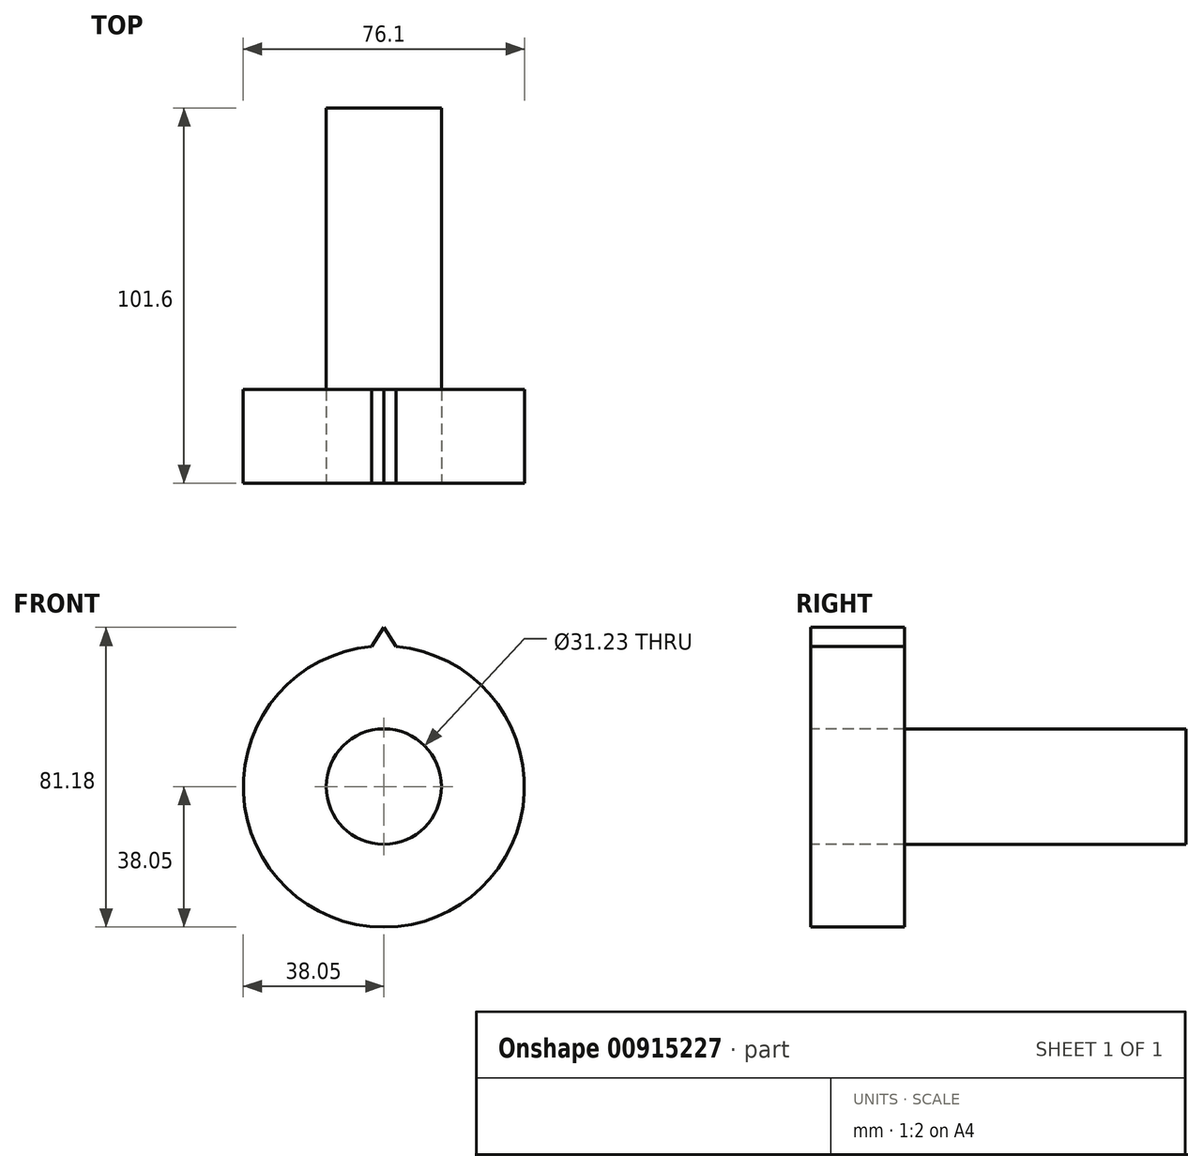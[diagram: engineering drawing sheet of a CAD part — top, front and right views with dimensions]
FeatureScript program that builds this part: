
annotation { "Feature Type Name" : "Feature", "Feature Type Description" : "" }
export const myFeature = defineFeature(function(context is Context, id is Id, definition is map)
    precondition{}
    {
        {
            var Q0;
            Q0=qCreatedBy(makeId("Front.planeOp"),FACE);
            var sketch = newSketch(context, id + "F0", { "sketchPlane" : qUnion([Q0])});
            skCircle(sketch, "E0", {"center": v(0, 0) * mm, "radius": 15.61 * mm});
            skSolve(sketch);
        }
        {
            var Q0;
            Q0 = qSketchRegion(id + "F0", true);
            extrude(context, id + "F1", {"entities" : qUnion([Q0]), "depth" : 101.6 * mm, "offsetDistance" : 25.4 * mm});
        }
        {
            var Q0;
            Q0=makeQuery(id+"F1.opExtrude","CAP_FACE",FACE,{"disambiguationData":[OSD([sQuery(id+"F0.wireOp",EDGE,"E0")])],"isStart":false});
            var sketch = newSketch(context, id + "F2", { "sketchPlane" : qUnion([Q0])});
            skCircle(sketch, "E1", {"center": v(0, 0) * mm, "radius": 15.61 * mm});
            skCircle(sketch, "E2", {"center": v(0, 0) * mm, "radius": 38.05 * mm});
            skSolve(sketch);
        }
        {
            var Q0;
            Q0=makeQuery(id+"F2.imprint","IMPRINT",FACE,{"disambiguationData":[TD([[makeQuery(id+"F2.imprint","IMPRINT",EDGE,{"derivedFrom":sQuery(id+"F2.wireOp",EDGE,"E1")}),-1.0]])]});
            extrude(context, id + "F3", {"entities" : qUnion([Q0]), "oppositeDirection" : true, "depth" : 25.4 * mm, "offsetDistance" : 25.4 * mm});
        }
        {
            var Q0;
            Q0=makeQuery(id+"F3.opExtrude","CAP_FACE",FACE,{"disambiguationData":[OSD([sQuery(id+"F2.wireOp",EDGE,"E1"),sQuery(id+"F2.wireOp",EDGE,"E2")])],"isStart":true});
            var sketch = newSketch(context, id + "F4", { "sketchPlane" : qUnion([Q0])});
            skLineSegment(sketch, "E3", {"start": v(-3.32, 37.9) * mm, "end": v(0, 43.13) * mm});
            skLineSegment(sketch, "E4", {"start": v(0, 43.13) * mm, "end": v(3.32, 37.9) * mm});
            skLineSegment(sketch, "E5", {"start": v(0, 0) * mm, "end": v(3.32, 37.9) * mm, "construction": true});
            skLineSegment(sketch, "E6", {"start": v(0, 0) * mm, "end": v(-3.32, 37.9) * mm, "construction": true});
            skLineSegment(sketch, "E7", {"start": v(-3.32, 37.9) * mm, "end": v(3.32, 37.9) * mm, "construction": true});
            skLineSegment(sketch, "E8", {"start": v(0, 0) * mm, "end": v(0, 37.9) * mm, "construction": true});
            skSolve(sketch);
        }
        {
            var Q0;
            {var subQ0=sQuery(id+"F4.wireOp",EDGE,"E3");Q0=makeQuery(id+"F4.imprint","IMPRINT",FACE,{"disambiguationData":[TD([[makeQuery(id+"F4.imprint","IMPRINT",EDGE,{"derivedFrom":subQ0}),-1.0]])]});}
            var Q1;
            Q1=makeQuery(id+"F3.opExtrude","CAP_FACE",FACE,{"disambiguationData":[OSD([sQuery(id+"F2.wireOp",EDGE,"E1"),sQuery(id+"F2.wireOp",EDGE,"E2")])],"isStart":false});
            extrude(context, id + "F5", {"entities" : qUnion([Q0]), "operationType" : NewBodyOperationType.ADD, "endBound" : BoundingType.UP_TO_SURFACE, "oppositeDirection" : true, "depth" : 25.4 * mm, "endBoundEntityFace" : qUnion([Q1]), "offsetDistance" : 25.4 * mm});
        }
    });
